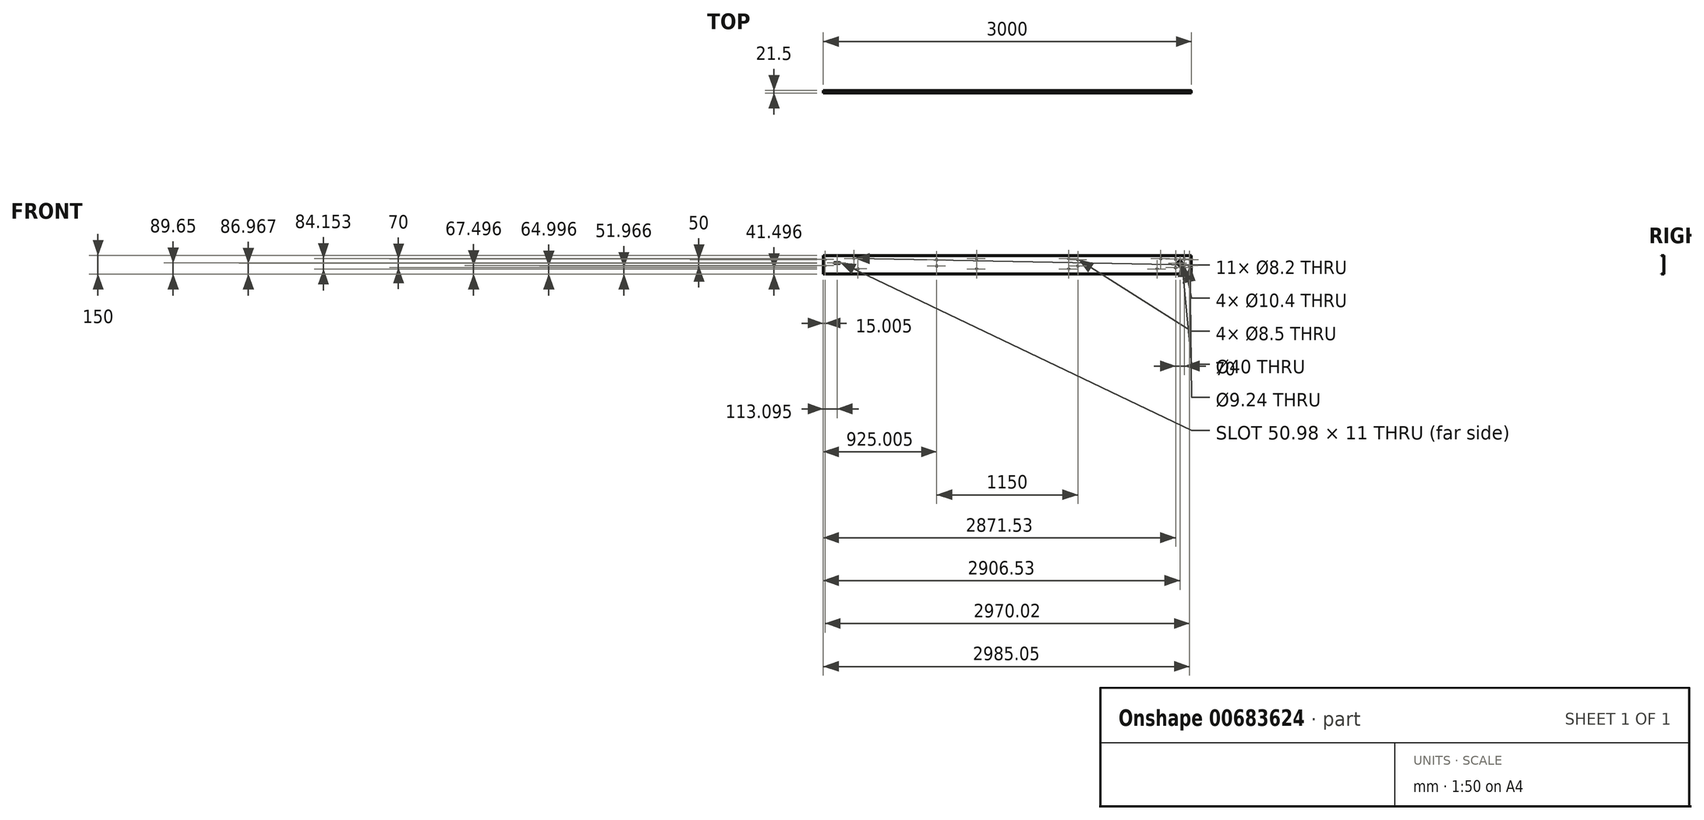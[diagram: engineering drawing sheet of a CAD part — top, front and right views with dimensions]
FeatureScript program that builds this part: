
annotation { "Feature Type Name" : "Feature", "Feature Type Description" : "" }
export const myFeature = defineFeature(function(context is Context, id is Id, definition is map)
    precondition{}
    {
        {
            var Q0;
            Q0=qCreatedBy(makeId("Front.planeOp"),FACE);
            var sketch = newSketch(context, id + "F0", { "sketchPlane" : qUnion([Q0])});
            skCircle(sketch, "E0", {"center": v(856.2, 112.55) * mm, "radius": 4.62 * mm});
            skCircle(sketch, "E1", {"center": v(621.15, 169.55) * mm, "radius": 4.1 * mm});
            skCircle(sketch, "E2", {"center": v(591.2, 86.55) * mm, "radius": 4.1 * mm});
            skCircle(sketch, "E3", {"center": v(777.68, 132.02) * mm, "radius": 20 * mm});
            skCircle(sketch, "E4", {"center": v(-878.85, 169.55) * mm, "radius": 4.1 * mm});
            skLineSegment(sketch, "E5", {"start": v(-1128.85, 195.05) * mm, "end": v(871.15, 195.05) * mm});
            skLineSegment(sketch, "E6", {"start": v(871.15, 195.05) * mm, "end": v(871.15, 45.05) * mm});
            skCircle(sketch, "E7", {"center": v(856.18, 162.55) * mm, "radius": 4.1 * mm});
            skCircle(sketch, "E8", {"center": v(-878.85, 86.55) * mm, "radius": 4.1 * mm});
            skCircle(sketch, "E9", {"center": v(-128.85, 169.55) * mm, "radius": 4.1 * mm});
            skCircle(sketch, "E10", {"center": v(-128.85, 86.55) * mm, "radius": 4.1 * mm});
            skCircle(sketch, "E11", {"center": v(742.68, 167.02) * mm, "radius": 5.2 * mm});
            skCircle(sketch, "E12", {"center": v(812.68, 167.02) * mm, "radius": 5.2 * mm});
            skCircle(sketch, "E13", {"center": v(742.68, 97.02) * mm, "radius": 5.2 * mm});
            skCircle(sketch, "E14", {"center": v(812.68, 97.02) * mm, "radius": 5.2 * mm});
            skLineSegment(sketch, "E15.0", {"start": v(-1128.85, 45.05) * mm, "end": v(871.15, 45.05) * mm});
            skPoint(sketch, "E16.orphan", {"position": v(871.15, 216.55) * mm});
            skPoint(sketch, "E17.orphan", {"position": v(871.15, 33.55) * mm});
            skLineSegment(sketch, "E18.0", {"start": v(-2128.85, 169.9) * mm, "end": v(-2128.85, 45.05) * mm});
            skLineSegment(sketch, "E19.0", {"start": v(-2128.85, 169.9) * mm, "end": v(-2128.85, 195.05) * mm});
            skLineSegment(sketch, "E20", {"start": v(-2128.85, 195.05) * mm, "end": v(-1128.85, 195.05) * mm});
            skLineSegment(sketch, "E21", {"start": v(-2128.85, 45.05) * mm, "end": v(-1128.85, 45.05) * mm});
            skCircle(sketch, "E22", {"center": v(-2113.85, 163.05) * mm, "radius": 4.1 * mm});
            skPoint(sketch, "E22.centerSnap0", {"position": v(-2128.85, 163.05) * mm});
            skCircle(sketch, "E23", {"center": v(-2113.85, 113.05) * mm, "radius": 4.1 * mm});
            skArc(sketch, "E24", {"start": v(-1995.28, 129.2) * mm, "mid": v(-1990.26, 135.14) * mm, "end": v(-1996.2, 140.16) * mm});
            skArc(sketch, "E25", {"start": v(-2035.75, 140.2) * mm, "mid": v(-2041.25, 134.7) * mm, "end": v(-2035.76, 129.2) * mm});
            skLineSegment(sketch, "E26", {"start": v(-2035.76, 129.2) * mm, "end": v(-1995.28, 129.2) * mm});
            skLineSegment(sketch, "E27", {"start": v(-2035.75, 140.2) * mm, "end": v(-1996.2, 140.16) * mm});
            skCircle(sketch, "E28", {"center": v(-1878.85, 170.7) * mm, "radius": 4.1 * mm});
            skCircle(sketch, "E29", {"center": v(-1845.85, 87.7) * mm, "radius": 4.1 * mm});
            skSolve(sketch);
        }
        {
            var Q0;
            Q0 = qSketchRegion(id + "F0", true);
            extrude(context, id + "F1", {"entities" : qUnion([Q0]), "depth" : 1.5 * mm, "offsetDistance" : 25 * mm});
        }
        {
            var Q0;
            Q0=makeQuery(id+"F1.opExtrude","CAP_FACE",FACE,{"disambiguationData":[OSD([sQuery(id+"F0.wireOp",EDGE,"E0"),sQuery(id+"F0.wireOp",EDGE,"E1"),sQuery(id+"F0.wireOp",EDGE,"E2"),sQuery(id+"F0.wireOp",EDGE,"E3"),sQuery(id+"F0.wireOp",EDGE,"E4"),sQuery(id+"F0.wireOp",EDGE,"E5"),sQuery(id+"F0.wireOp",EDGE,"31fbd005-371a-4950-9023-6bd7900d5322"),sQuery(id+"F0.wireOp",EDGE,"E6"),sQuery(id+"F0.wireOp",EDGE,"E7"),sQuery(id+"F0.wireOp",EDGE,"da52ceb5-953a-4911-b880-2813699d4ba7"),sQuery(id+"F0.wireOp",EDGE,"27c3eecb-02c1-45e1-8efc-a86d12ded6dc"),sQuery(id+"F0.wireOp",EDGE,"e9ae3657-2029-40e5-b887-3879fb827f7b"),sQuery(id+"F0.wireOp",EDGE,"E8"),sQuery(id+"F0.wireOp",EDGE,"E9"),sQuery(id+"F0.wireOp",EDGE,"E10"),sQuery(id+"F0.wireOp",EDGE,"E11"),sQuery(id+"F0.wireOp",EDGE,"E12"),sQuery(id+"F0.wireOp",EDGE,"E13"),sQuery(id+"F0.wireOp",EDGE,"E14"),sQuery(id+"F0.wireOp",EDGE,"E15.0")])],"isStart":false});
            var sketch = newSketch(context, id + "F2", { "sketchPlane" : qUnion([Q0])});
            skLineSegment(sketch, "E30.bottom", {"start": v(871.15, 195.05) * mm, "end": v(-2128.85, 195.05) * mm});
            skLineSegment(sketch, "E30.top", {"start": v(871.15, 193.55) * mm, "end": v(-2128.85, 193.55) * mm});
            skLineSegment(sketch, "E30.left", {"start": v(871.15, 195.05) * mm, "end": v(871.15, 193.55) * mm});
            skLineSegment(sketch, "E30.right", {"start": v(-2128.85, 195.05) * mm, "end": v(-2128.85, 193.55) * mm});
            skLineSegment(sketch, "E31.bottom", {"start": v(871.15, 45.05) * mm, "end": v(-2128.85, 45.05) * mm});
            skLineSegment(sketch, "E31.top", {"start": v(871.15, 46.55) * mm, "end": v(-2128.85, 46.55) * mm});
            skLineSegment(sketch, "E31.left", {"start": v(871.15, 45.05) * mm, "end": v(871.15, 46.55) * mm});
            skLineSegment(sketch, "E31.right", {"start": v(-2128.85, 45.05) * mm, "end": v(-2128.85, 46.55) * mm});
            skSolve(sketch);
        }
        {
            var Q0;
            Q0 = qSketchRegion(id + "F2", true);
            extrude(context, id + "F3", {"entities" : qUnion([Q0]), "operationType" : NewBodyOperationType.ADD, "depth" : 20 * mm, "offsetDistance" : 25 * mm});
        }
        {
            var Q0;
            Q0=makeQuery(id+"F3.opExtrude","CAP_EDGE",EDGE,{"disambiguationData":[OSD([sQuery(id+"F2.wireOp",EDGE,"E30.top")])],"isStart":true});
            var Q1;
            Q1=makeQuery(id+"F1.opExtrude","CAP_EDGE",EDGE,{"disambiguationData":[OSD([sQuery(id+"F0.wireOp",EDGE,"E15.0")])],"isStart":true});
            var Q2;
            Q2=makeQuery(id+"F3.opExtrude","CAP_EDGE",EDGE,{"disambiguationData":[OSD([sQuery(id+"F2.wireOp",EDGE,"E31.top")])],"isStart":true});
            var Q3;
            Q3=makeQuery(id+"F1.opExtrude","CAP_EDGE",EDGE,{"disambiguationData":[OSD([sQuery(id+"F0.wireOp",EDGE,"E5")])],"isStart":true});
            fillet(context, id + "F4", {"entities" : qUnion([Q0, Q1, Q2, Q3]), "radius" : .5 * mm, "tangentPropagation" : true, "allowEdgeOverflow" : false});
        }
        {
            var Q0;
            Q0=makeQuery(id+"F1.opExtrude","CAP_FACE",FACE,{"disambiguationData":[OSD([sQuery(id+"F0.wireOp",EDGE,"E0"),sQuery(id+"F0.wireOp",EDGE,"E1"),sQuery(id+"F0.wireOp",EDGE,"E2"),sQuery(id+"F0.wireOp",EDGE,"E3"),sQuery(id+"F0.wireOp",EDGE,"E4"),sQuery(id+"F0.wireOp",EDGE,"E5"),sQuery(id+"F0.wireOp",EDGE,"E6"),sQuery(id+"F0.wireOp",EDGE,"E7"),sQuery(id+"F0.wireOp",EDGE,"E8"),sQuery(id+"F0.wireOp",EDGE,"E9"),sQuery(id+"F0.wireOp",EDGE,"E10"),sQuery(id+"F0.wireOp",EDGE,"E11"),sQuery(id+"F0.wireOp",EDGE,"E12"),sQuery(id+"F0.wireOp",EDGE,"E13"),sQuery(id+"F0.wireOp",EDGE,"E14"),sQuery(id+"F0.wireOp",EDGE,"E15.0"),sQuery(id+"F0.wireOp",EDGE,"E18.0"),sQuery(id+"F0.wireOp",EDGE,"E19.0"),sQuery(id+"F0.wireOp",EDGE,"E20"),sQuery(id+"F0.wireOp",EDGE,"E21"),sQuery(id+"F0.wireOp",EDGE,"E22"),sQuery(id+"F0.wireOp",EDGE,"E23"),sQuery(id+"F0.wireOp",EDGE,"E24"),sQuery(id+"F0.wireOp",EDGE,"E25"),sQuery(id+"F0.wireOp",EDGE,"E26"),sQuery(id+"F0.wireOp",EDGE,"E27"),sQuery(id+"F0.wireOp",EDGE,"E28"),sQuery(id+"F0.wireOp",EDGE,"E29")])],"isStart":true});
            var sketch = newSketch(context, id + "F5", { "sketchPlane" : qUnion([Q0])});
            skCircle(sketch, "E32", {"center": v(1203.85, 160.05) * mm, "radius": 4.25 * mm});
            skCircle(sketch, "E33", {"center": v(1203.85, 110.05) * mm, "radius": 4.25 * mm});
            skLineSegment(sketch, "E34", {"start": v(628.85, 194.55) * mm, "end": v(628.85, 45.55) * mm});
            skCircle(sketch, "E35.MirrorC", {"center": v(53.85, 160.05) * mm, "radius": 4.25 * mm});
            skCircle(sketch, "E36.MirrorC", {"center": v(53.85, 110.05) * mm, "radius": 4.25 * mm});
            skSolve(sketch);
        }
        {
            var Q0;
            Q0 = qSketchRegion(id + "F5", true);
            extrude(context, id + "F6", {"entities" : qUnion([Q0]), "operationType" : NewBodyOperationType.REMOVE, "endBound" : BoundingType.THROUGH_ALL, "oppositeDirection" : true, "depth" : 25 * mm, "offsetDistance" : 25 * mm});
        }
        {
            var Q0;
            Q0=makeQuery(id+"F3.boolean.opBoolean","MERGE",FACE,{"derivedFrom":[makeQuery(id+"F1.opExtrude","SWEPT_FACE",FACE,{"disambiguationData":[OSD([sQuery(id+"F0.wireOp",EDGE,"E5"),sQuery(id+"F0.wireOp",EDGE,"E20")])]}),makeQuery(id+"F3.opExtrude","SWEPT_FACE",FACE,{"disambiguationData":[OSD([sQuery(id+"F2.wireOp",EDGE,"E30.bottom")])]})]});
            var sketch = newSketch(context, id + "F7", { "sketchPlane" : qUnion([Q0])});
            skLineSegment(sketch, "E37.bottom", {"start": v(836.15, -21.5) * mm, "end": v(761.15, -21.5) * mm});
            skLineSegment(sketch, "E37.top", {"start": v(836.15, -0.5) * mm, "end": v(761.15, -0.5) * mm});
            skLineSegment(sketch, "E37.left", {"start": v(836.15, -21.5) * mm, "end": v(836.15, -0.5) * mm});
            skLineSegment(sketch, "E37.right", {"start": v(761.15, -21.5) * mm, "end": v(761.15, -0.5) * mm});
            skLineSegment(sketch, "E38.bottom", {"start": v(-2093.85, -21.5) * mm, "end": v(-2018.85, -21.5) * mm});
            skLineSegment(sketch, "E38.top", {"start": v(-2093.85, -0.5) * mm, "end": v(-2018.85, -0.5) * mm});
            skLineSegment(sketch, "E38.left", {"start": v(-2093.85, -21.5) * mm, "end": v(-2093.85, -0.5) * mm});
            skLineSegment(sketch, "E38.right", {"start": v(-2018.85, -21.5) * mm, "end": v(-2018.85, -0.5) * mm});
            skSolve(sketch);
        }
        {
            var Q0;
            Q0=makeQuery(id+"F7.imprint","IMPRINT",FACE,{"disambiguationData":[TD([[makeQuery(id+"F7.imprint","IMPRINT",EDGE,{"derivedFrom":sQuery(id+"F7.wireOp",EDGE,"E37.bottom")}),1.0]])]});
            var Q1;
            Q1=makeQuery(id+"F7.imprint","IMPRINT",FACE,{"disambiguationData":[TD([[makeQuery(id+"F7.imprint","IMPRINT",EDGE,{"derivedFrom":sQuery(id+"F7.wireOp",EDGE,"E38.bottom")}),1.0]])]});
            extrude(context, id + "F8", {"entities" : qUnion([Q0, Q1]), "operationType" : NewBodyOperationType.REMOVE, "oppositeDirection" : true, "depth" : 1.5 * mm, "offsetDistance" : 25 * mm});
        }
    });
